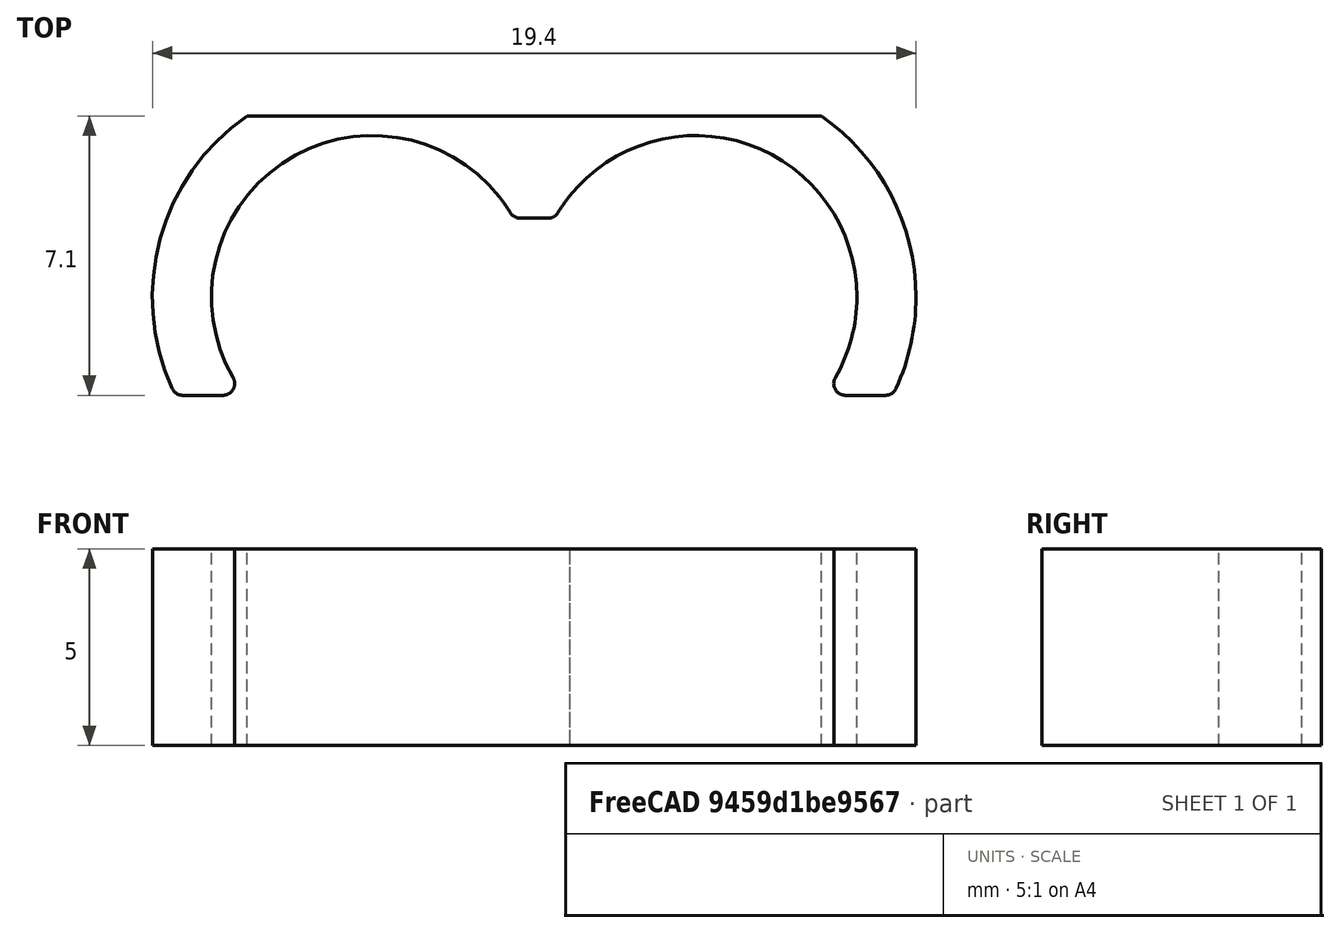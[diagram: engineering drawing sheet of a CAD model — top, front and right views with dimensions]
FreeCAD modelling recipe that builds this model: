
FCSTD DOCUMENT  (FreeCAD 0.18.4R)
Label: CapClip3
License: All rights reserved
LicenseURL: http://en.wikipedia.org/wiki/All_rights_reserved
objects: Part::Box×5, Part::Cut×5, Part::Cylinder×4, Part::MultiFuse×3, Part::Fillet×2, Mesh::Feature×1
note: 19 computed .brp shape members not serialized (recipe doc carries the construction recipe); baked Part::Feature solids carry a one-line shape summary decoded from their .brp

FEATURE [Part::Box] Box  label="Würfel"
  AttacherType = Attacher::AttachEngine3D
  Height = 1
  Length = 15
  Placement = pos=(-3.5,0,-5.6) rot=(0,0,1;0rad)
  Width = 5
FEATURE [Part::Cylinder] Cylinder  label="Zylinder"
  Angle = 360
  AttacherType = Attacher::AttachEngine3D
  Height = 5
  Radius = 5.6
FEATURE [Part::Cylinder] Cylinder001  label="Zylinder001"
  Angle = 360
  AttacherType = Attacher::AttachEngine3D
  Height = 5
  Radius = 4.1
FEATURE [Part::Box] Box001  label="Würfel001"
  AttacherType = Attacher::AttachEngine3D
  Height = 5
  Length = 12
  Placement = pos=(-6,-12.5,0) rot=(0,0,1;0rad)
  Width = 10
FEATURE [Part::Box] Box002  label="Würfel002"
  AttacherType = Attacher::AttachEngine3D
  Height = 5
  Length = 10
  Placement = pos=(0,-8,0) rot=(0,0,1;0rad)
  Width = 10
FEATURE [Part::Cylinder] Cylinder002  label="Zylinder002"
  Angle = 360
  AttacherType = Attacher::AttachEngine3D
  Height = 5
  Placement = pos=(8.2,0,0) rot=(0,0,1;0rad)
  Radius = 4.1
FEATURE [Part::Cylinder] Cylinder003  label="Zylinder003"
  Angle = 360
  AttacherType = Attacher::AttachEngine3D
  Height = 5
  Placement = pos=(8.2,0,0) rot=(0,0,1;0rad)
  Radius = 5.6
FEATURE [Part::Box] Box003  label="Würfel003"
  AttacherType = Attacher::AttachEngine3D
  Height = 5
  Length = 12
  Placement = pos=(2,-12.5,0) rot=(0,0,1;0rad)
  Width = 10
FEATURE [Part::Cut] Cut
  Base = -> Cylinder003
  Tool = -> Box003
FEATURE [Part::Cut] Cut001
  Base = -> Cylinder
  Tool = -> Box001
FEATURE [Part::MultiFuse] Fusion
  Shapes = -> [Cut,Cut001]
FEATURE [Part::Cut] Cut002
  Base = -> Fusion
  Tool = -> Box002
FEATURE [Part::MultiFuse] Fusion001
  Shapes = -> [Cylinder001,Cylinder002]
FEATURE [Part::Cut] Cut003
  Base = -> Cut002
  Tool = -> Fusion001
FEATURE [Part::Fillet] Fillet
  Base = -> Cut003
  Edges = 2 edges r=0.3: [Edge22,Edge35]
FEATURE [Part::Fillet] Fillet001
  Base = -> Fillet
  Edges = 4 edges r=0.3: [Edge25,Edge34,Edge38,Edge41]
  Placement = pos=(0,0,0) rot=(-1,0,0;1.5708rad)
FEATURE [Part::Box] Box004  label="Würfel004"
  AttacherType = Attacher::AttachEngine3D
  Height = 2
  Length = 2
  Placement = pos=(3,0,-5) rot=(0,0,1;0rad)
  Width = 5
FEATURE [Part::MultiFuse] Fusion002
  Shapes = -> [Fillet001,Box004]
FEATURE [Part::Cut] Cut004
  Base = -> Fusion002
  Placement = pos=(0,0,0) rot=(1,0,0;1.5708rad)
  Tool = -> Box
FEATURE [Mesh::Feature] Mesh  label="Cut004 (Meshed)"
